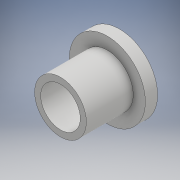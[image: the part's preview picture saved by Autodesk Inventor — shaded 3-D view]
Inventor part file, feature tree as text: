
AUTODESK INVENTOR PART (.ipt)
format: ipt  version: 2017 (Build 210142000, 142)  size: 117,760 bytes
history: native  units: mm
features: extrude x3, sketch x3
ambient origin geometry x8: Origin, YZ Plane, XZ Plane, XY Plane, X Axis, Y Axis, Z Axis, Center Point
bodies: Body1 (feature_tree)
feature tree (6):
  extrude  "Extrusion3"  Depth=6.0mm
  extrude  "Extrusion4"  Depth=4.0mm
  extrude  "Extrusion5"  Depth=10.0mm
  sketch  "Sketch3"  dims[d8=25.0mm d9=6.0mm]
  sketch  "Sketch4"  dims[d10=4.0mm d11=0.0mm d12=2.0mm]
  sketch  "Sketch5"  dims[d13=10.0mm d14=0.0mm d15=2.0mm d16=5.4mm d17=0.0mm]
